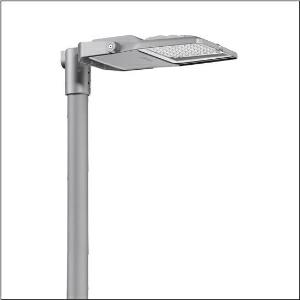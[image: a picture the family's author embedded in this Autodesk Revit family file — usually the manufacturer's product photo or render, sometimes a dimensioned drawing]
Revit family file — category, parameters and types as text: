
# Revit family: floodlight_fl_21_iq_mini___pl52_5xa7772b4d3a_2373
name_source: partatom
category: Lighting Fixtures
units: mm (PartAtom-declared; Revit-internal decimal feet)

## family parameters
Cut with Voids When Loaded = No
Host = Face
Light Source = No
Part Type = Normal
Room Calculation Point = No
Round Connector Dimension = Use Diameter
Shared = No

## types (1)
- --- (1 x LED, 6490 lm, 45.5 W, 4000K)
    Apparent Load = 46 VA
    CIE Flux Codes = 26 60 98 100 100
    Color Rendering = 70
    Color Temperature = 4000K
    Default Elevation = 1800 mm
    Description = Floodlight FL 21 iQ mini, floodlight, primary light control with lens, of PMMA, primary optical cover: protective disc, of toughened safety glass, transparent, light distribution: PL52, light emission: direct distribution, installation type: surface-mounted, LED, High Power LED, rated luminous flux: 6.490lm, luminous efficacy: 143lm/W, light colour: 740, colour temperature: 4000K, control: Auto-Match, Temp-Guard, Night-Set, Smart-Wire, Desk-Remote (wireless, voltage-free reading and setting of iQ features in the workshop via application-optimized NFC function/RFID function), optimised constant luminous flux control (CLO 2.0), Light-Fading, Lumen-Switch, with terminal, 6-pole, mains connection: 220..240V, AC, 50/60Hz, start of lifetime: 46W, end of service life: 48W, reduction: 22W, luminaire housing, of diecast aluminium, powder-coated, Siteco® metallic grey (DB 702S), corrosivity category C5 mid according to DIN EN ISO 12944, sealing non-destructively replaceable, please order mast flange separately, mast bracket, of steel, galvanised, powder-coated, protection rating (complete): IP66, insulation class (complete): insulation class II (safety insulation), certification: CE, ENEC, VDE, protection symbol: D, impact resistance: IK08, permissible operating ambient temperature: -40..+40°C, permissible operating ambient temperature for outdoor applications: -40..+50°C, standard: DIN EN 12944, LABS conformity tested according to VDMA 24364:2018-05, packaging unit: 1 piece

Light Distribution: PL52
    Height = 70 mm
    Lamp = 1 x LED
    Lamp Light Flux = 6490 lm
    Lamp Power = 45.5 W
    Lamp count = 1
    Length = 485 mm
    Luminous efficacy = 143 lm/W
    Manufacturer = Siteco
    ModVariant = No
    Model = 5XA7772B4D3A
    Number of Poles = 1
    OnlyDefault = Yes
    Power Factor = 1
    Product Name = Floodlight FL 21 iQ mini | PL52
    Product group = floodlight | pylon annexe
    ProductGroupID = 6200
    Protection Class = Protection class II
    Protection Degree = IP 66
    RLX_Detail_Level = 1
    RLX_Emergency_Light_Flux = 0 lm
    RLX_Emergency_Type = 0
    RLX_Emergency_Type_DB = No
    RlxData = <blob elided: 101293 chars, md5=50a8614a>
    Socket = socket
    Standby Power = 0 W
    System Light Flux = 6490 lm
    System Power = 46 W
    Type Comments = factory setting: luminous flux: 100 % | dim-lin: 254 | 463 mA
    Type Image = l_1007125.jpg
    URL = http://relux.com
    VarID = @adj_135033
    Voltage = 0 V
    Weight = 0.00 kg
    Width = 337 mm

## geometry (parser evidence)
native form markers: Blend x4, Sweep x13
no freeform markers — native parametric forms only
